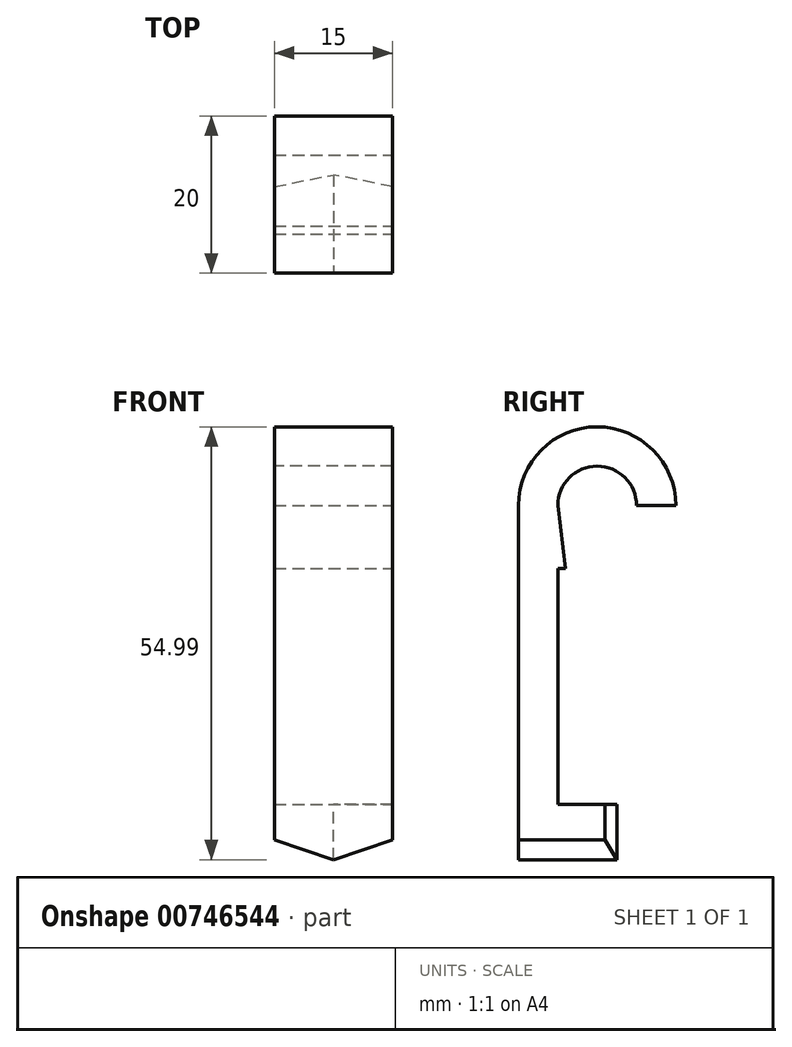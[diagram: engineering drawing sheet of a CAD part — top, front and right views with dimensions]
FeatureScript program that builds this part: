
annotation { "Feature Type Name" : "Feature", "Feature Type Description" : "" }
export const myFeature = defineFeature(function(context is Context, id is Id, definition is map)
    precondition{}
    {
        {
            var Q0;
            Q0=qCreatedBy(makeId("Top.planeOp"),FACE);
            var sketch = newSketch(context, id + "F0", { "sketchPlane" : qUnion([Q0])});
            skLineSegment(sketch, "E0.bottom", {"start": v(-7.5, 5) * mm, "end": v(7.5, 5) * mm});
            skLineSegment(sketch, "E0.top", {"start": v(-7.5, 0) * mm, "end": v(7.5, 0) * mm});
            skLineSegment(sketch, "E0.left", {"start": v(-7.5, 5) * mm, "end": v(-7.5, 0) * mm});
            skLineSegment(sketch, "E0.right", {"start": v(7.5, 5) * mm, "end": v(7.5, 0) * mm});
            skPoint(sketch, "E1", {"position": v(0, 0) * mm});
            skSolve(sketch);
        }
        {
            var Q0;
            Q0=makeQuery(id+"F0.imprint","IMPRINT",FACE,{"disambiguationData":[TD([[makeQuery(id+"F0.imprint","IMPRINT",EDGE,{"derivedFrom":sQuery(id+"F0.wireOp",EDGE,"E0.bottom")}),-1.0]])]});
            extrude(context, id + "F1", {"entities" : qUnion([Q0]), "depth" : 38 * mm, "offsetDistance" : 25 * mm});
        }
        {
            var Q0;
            Q0=makeQuery(id+"F1.opExtrude","CAP_FACE",FACE,{"disambiguationData":[OSD([sQuery(id+"F0.wireOp",EDGE,"E0.bottom"),sQuery(id+"F0.wireOp",EDGE,"E0.top"),sQuery(id+"F0.wireOp",EDGE,"E0.left"),sQuery(id+"F0.wireOp",EDGE,"E0.right")])],"isStart":true});
            var sketch = newSketch(context, id + "F2", { "sketchPlane" : qUnion([Q0])});
            skLineSegment(sketch, "E2.bottom", {"start": v(7.5, 0) * mm, "end": v(-7.5, 0) * mm});
            skLineSegment(sketch, "E2.top", {"start": v(7.5, -10) * mm, "end": v(-7.5, -10) * mm, "construction": true});
            skLineSegment(sketch, "E2.left", {"start": v(7.5, 0) * mm, "end": v(7.5, -10) * mm});
            skLineSegment(sketch, "E2.right", {"start": v(-7.5, 0) * mm, "end": v(-7.5, -10) * mm});
            skLineSegment(sketch, "E3", {"start": v(-12.5, -10) * mm, "end": v(12.5, -10) * mm, "construction": true});
            skPoint(sketch, "E4", {"position": v(0, -10) * mm});
            skLineSegment(sketch, "E5", {"start": v(-12.5, -10) * mm, "end": v(0, -12.5) * mm, "construction": true});
            skLineSegment(sketch, "E6", {"start": v(0, -12.5) * mm, "end": v(12.5, -10) * mm, "construction": true});
            skLineSegment(sketch, "E7", {"start": v(-7.5, -10) * mm, "end": v(-7.5, -11) * mm});
            skLineSegment(sketch, "E8", {"start": v(7.5, -10) * mm, "end": v(7.5, -11) * mm});
            skLineSegment(sketch, "E9", {"start": v(7.5, -11) * mm, "end": v(0, -12.5) * mm});
            skLineSegment(sketch, "E10", {"start": v(-7.5, -11) * mm, "end": v(0, -12.5) * mm});
            skLineSegment(sketch, "E11", {"start": v(0, -12.5) * mm, "end": v(0, -10) * mm, "construction": true});
            skSolve(sketch);
        }
        {
            var Q0;
            {var subQ0=sQuery(id+"F2.wireOp",EDGE,"E2.top");Q0=makeQuery(id+"F2.imprint","IMPRINT",FACE,{"disambiguationData":[TD([[makeQuery(id+"F2.imprint","IMPRINT",EDGE,{"derivedFrom":subQ0}),-1.0]])]});}
            var Q1;
            {var subQ0=sQuery(id+"F2.wireOp",EDGE,"E2.bottom");Q1=makeQuery(id+"F2.imprint","IMPRINT",FACE,{"disambiguationData":[TD([[makeQuery(id+"F2.imprint","IMPRINT",EDGE,{"derivedFrom":subQ0}),-1.0]])]});}
            var Q2;
            {var subQ0=sQuery(id+"F2.wireOp",EDGE,"E7");Q2=makeQuery(id+"F2.imprint","IMPRINT",FACE,{"disambiguationData":[TD([[makeQuery(id+"F2.imprint","IMPRINT",EDGE,{"derivedFrom":subQ0}),1.0]])]});}
            extrude(context, id + "F3", {"entities" : qUnion([Q0, Q1, Q2]), "operationType" : NewBodyOperationType.ADD, "depth" : 7 * mm, "offsetDistance" : 25 * mm});
        }
        {
            var Q0;
            Q0=makeQuery(id+"F3.opExtrude","CAP_EDGE",EDGE,{"disambiguationData":[OSD([sQuery(id+"F2.wireOp",EDGE,"E2.right"),sQuery(id+"F2.wireOp",EDGE,"E7")])],"isStart":false});
            var Q1;
            Q1=makeQuery(id+"F3.opExtrude","CAP_EDGE",EDGE,{"disambiguationData":[OSD([sQuery(id+"F2.wireOp",EDGE,"E2.left"),sQuery(id+"F2.wireOp",EDGE,"E8")])],"isStart":false});
            chamfer(context, id + "F4", {"entities" : qUnion([Q0, Q1]), "chamferType" : ChamferType.OFFSET_ANGLE, "width" : 2.5 * mm, "oppositeDirection" : false, "angle" : 71.6 * degree, "tangentPropagation" : true});
        }
        {
            var Q0;
            Q0=makeQuery(id+"F3.boolean.opBoolean","MERGE",FACE,{"derivedFrom":[makeQuery(id+"F1.opExtrude","SWEPT_FACE",FACE,{"disambiguationData":[OSD([sQuery(id+"F0.wireOp",EDGE,"E0.right")])]}),makeQuery(id+"F3.opExtrude","SWEPT_FACE",FACE,{"disambiguationData":[OSD([sQuery(id+"F2.wireOp",EDGE,"E2.left"),sQuery(id+"F2.wireOp",EDGE,"E8")])]})]});
            var sketch = newSketch(context, id + "F5", { "sketchPlane" : qUnion([Q0])});
            skPoint(sketch, "E12.startSnap0", {"position": v(2.5, 38) * mm});
            skArc(sketch, "E13", {"start": v(17.5, 38) * mm, "mid": v(10, 45.5) * mm, "end": v(2.5, 38) * mm});
            skLineSegment(sketch, "E14", {"start": v(2.5, 38) * mm, "end": v(5, 38) * mm, "construction": true});
            skLineSegment(sketch, "E15", {"start": v(17.5, 38) * mm, "end": v(15, 38) * mm, "construction": true});
            skLineSegment(sketch, "E16", {"start": v(15, 38) * mm, "end": v(5, 38) * mm, "construction": true});
            skSolve(sketch);
        }
        {
            var Q0;
            Q0=makeQuery(id+"F1.opExtrude","CAP_FACE",FACE,{"disambiguationData":[OSD([sQuery(id+"F0.wireOp",EDGE,"E0.bottom"),sQuery(id+"F0.wireOp",EDGE,"E0.top"),sQuery(id+"F0.wireOp",EDGE,"E0.left"),sQuery(id+"F0.wireOp",EDGE,"E0.right")])],"isStart":false});
            var Q1;
            Q1=sQuery(id+"F5.wireOp",EDGE,"E13");
            sweep(context, id + "F6", {"operationType" : NewBodyOperationType.ADD, "profiles" : qUnion([Q0]), "path" : qUnion([Q1])});
        }
        {
            var Q0;
            {var subQ0=sQuery(id+"F0.wireOp",EDGE,"E0.right");Q0=makeQuery(id+"F6.boolean.opBoolean","MERGE",FACE,{"derivedFrom":[makeQuery(id+"F3.boolean.opBoolean","MERGE",FACE,{"derivedFrom":[makeQuery(id+"F1.opExtrude","SWEPT_FACE",FACE,{"disambiguationData":[OSD([subQ0])]}),makeQuery(id+"F3.opExtrude","SWEPT_FACE",FACE,{"disambiguationData":[OSD([sQuery(id+"F2.wireOp",EDGE,"E2.left"),sQuery(id+"F2.wireOp",EDGE,"E8")])]})]}),makeQuery(id+"F6.opSweep","SWEPT_FACE",FACE,{"disambiguationData":[OSD([subQ0,sQuery(id+"F5.wireOp",EDGE,"E13")])]})]});}
            var sketch = newSketch(context, id + "F7", { "sketchPlane" : qUnion([Q0])});
            skLineSegment(sketch, "E17", {"start": v(5, 38) * mm, "end": v(5, 30) * mm});
            skLineSegment(sketch, "E18", {"start": v(5, 30) * mm, "end": v(6, 30) * mm});
            skLineSegment(sketch, "E19", {"start": v(6, 30) * mm, "end": v(5, 38) * mm});
            skSolve(sketch);
        }
        {
            var Q0;
            Q0 = qSketchRegion(id + "F7", true);
            extrude(context, id + "F8", {"entities" : qUnion([Q0]), "operationType" : NewBodyOperationType.ADD, "oppositeDirection" : true, "depth" : 15 * mm, "offsetDistance" : 25 * mm});
        }
    });
